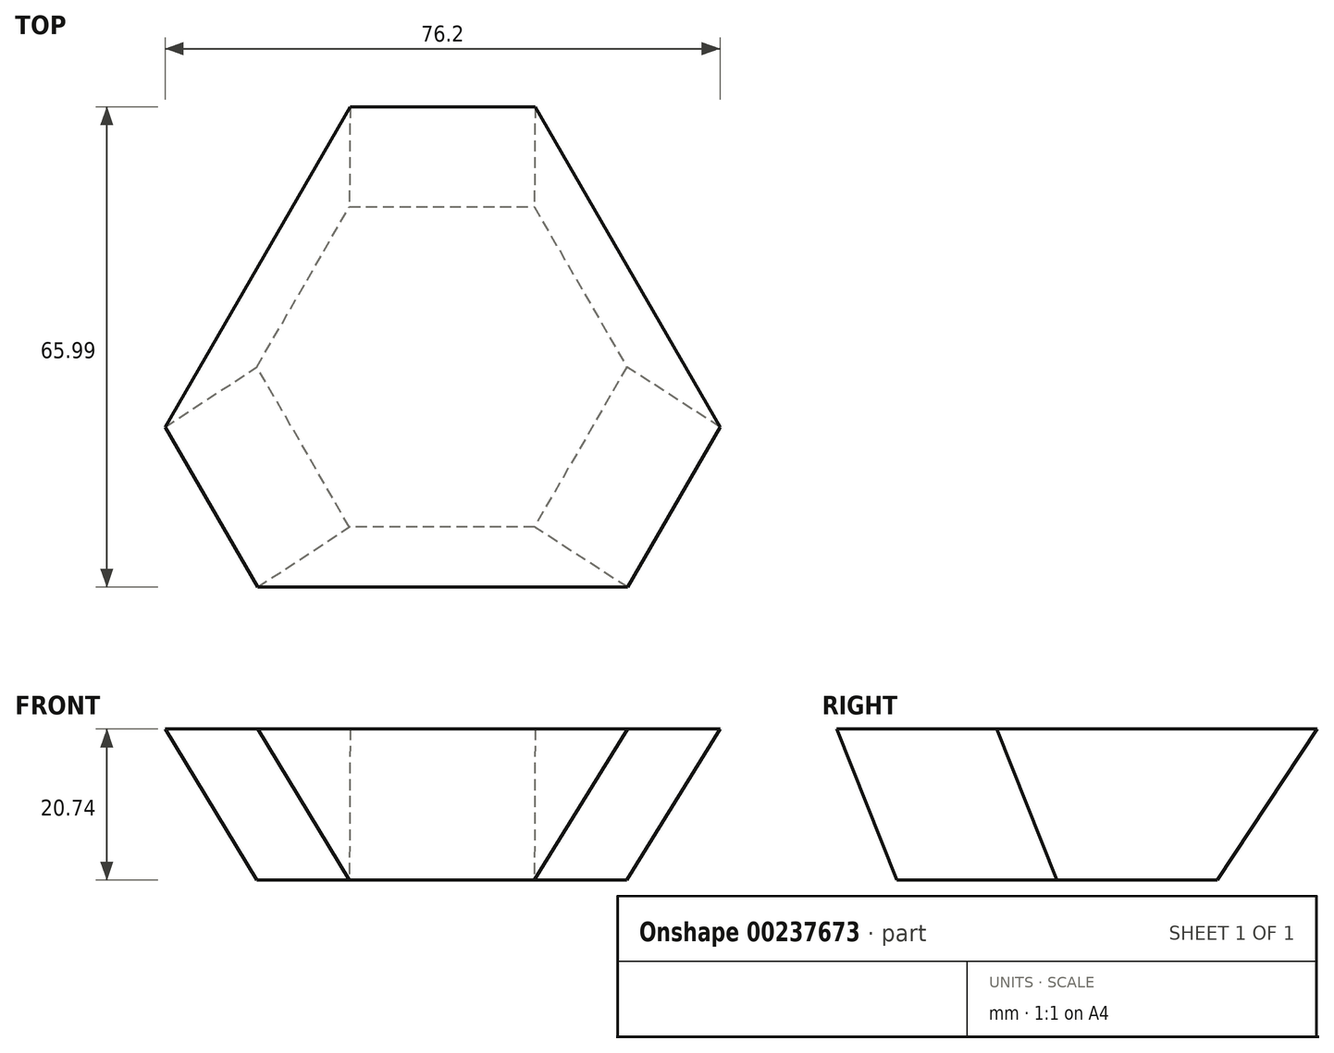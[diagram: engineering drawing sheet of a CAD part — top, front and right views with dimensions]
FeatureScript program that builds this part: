
annotation { "Feature Type Name" : "Feature", "Feature Type Description" : "" }
export const myFeature = defineFeature(function(context is Context, id is Id, definition is map)
    precondition{}
    {
        {
            var Q0;
            Q0=qCreatedBy(makeId("Top.planeOp"),FACE);
            var sketch = newSketch(context, id + "F0", { "sketchPlane" : qUnion([Q0])});
            skCircle(sketch, "E0.cCircle", {"center": v(0, 0) * mm, "radius": 25.4 * mm, "construction": true});
            skLineSegment(sketch, "E0.0", {"start": v(25.4, 0) * mm, "end": v(12.7, -22) * mm});
            skLineSegment(sketch, "E0.1", {"start": v(12.7, -22) * mm, "end": v(-12.7, -22) * mm});
            skLineSegment(sketch, "E0.2", {"start": v(-12.7, -22) * mm, "end": v(-25.4, 0) * mm});
            skLineSegment(sketch, "E0.3", {"start": v(-25.4, 0) * mm, "end": v(-12.7, 22) * mm});
            skLineSegment(sketch, "E0.4", {"start": v(-12.7, 22) * mm, "end": v(12.7, 22) * mm});
            skLineSegment(sketch, "E0.5", {"start": v(12.7, 22) * mm, "end": v(25.4, 0) * mm});
            skSolve(sketch);
        }
        {
            var Q0;
            Q0=qCreatedBy(makeId("Top.planeOp"),FACE);
            cPlane(context, id + "F1", {"entities" : qUnion([Q0]), "cplaneType" : CPlaneType.OFFSET, "offset" : 20.74 * mm, "width" : 152.4 * mm, "height" : 152.4 * mm});
        }
        {
            var Q0;
            Q0=qCreatedBy(id+"F1.planeOp",FACE);
            var sketch = newSketch(context, id + "F2", { "sketchPlane" : qUnion([Q0])});
            skLineSegment(sketch, "E1", {"start": v(-12.6, 35.73) * mm, "end": v(12.8, 35.73) * mm});
            skLineSegment(sketch, "E2", {"start": v(12.8, 35.73) * mm, "end": v(38.2, -8.27) * mm});
            skLineSegment(sketch, "E3", {"start": v(38.2, -8.27) * mm, "end": v(25.5, -30.26) * mm});
            skLineSegment(sketch, "E4", {"start": v(25.5, -30.26) * mm, "end": v(-25.3, -30.26) * mm});
            skLineSegment(sketch, "E5", {"start": v(-25.3, -30.26) * mm, "end": v(-38, -8.27) * mm});
            skLineSegment(sketch, "E6", {"start": v(-38, -8.27) * mm, "end": v(-12.6, 35.73) * mm});
            skPoint(sketch, "E7.first.point", {"position": v(-25.94, 12.62) * mm});
            skPoint(sketch, "E7.second.point", {"position": v(25.5, 13.73) * mm});
            skPoint(sketch, "E7.third.point", {"position": v(0, -30.26) * mm});
            skSolve(sketch);
        }
        {
            var Q0;
            Q0 = qSketchRegion(id + "F2", true);
            var Q1;
            Q1 = qSketchRegion(id + "F0", true);
            loft(context, id + "F3", {"sheetProfilesArray" : [{ "sheetProfileEntities" : qUnion([Q0]) }, { "sheetProfileEntities" : qUnion([Q1]) }]});
        }
    });
